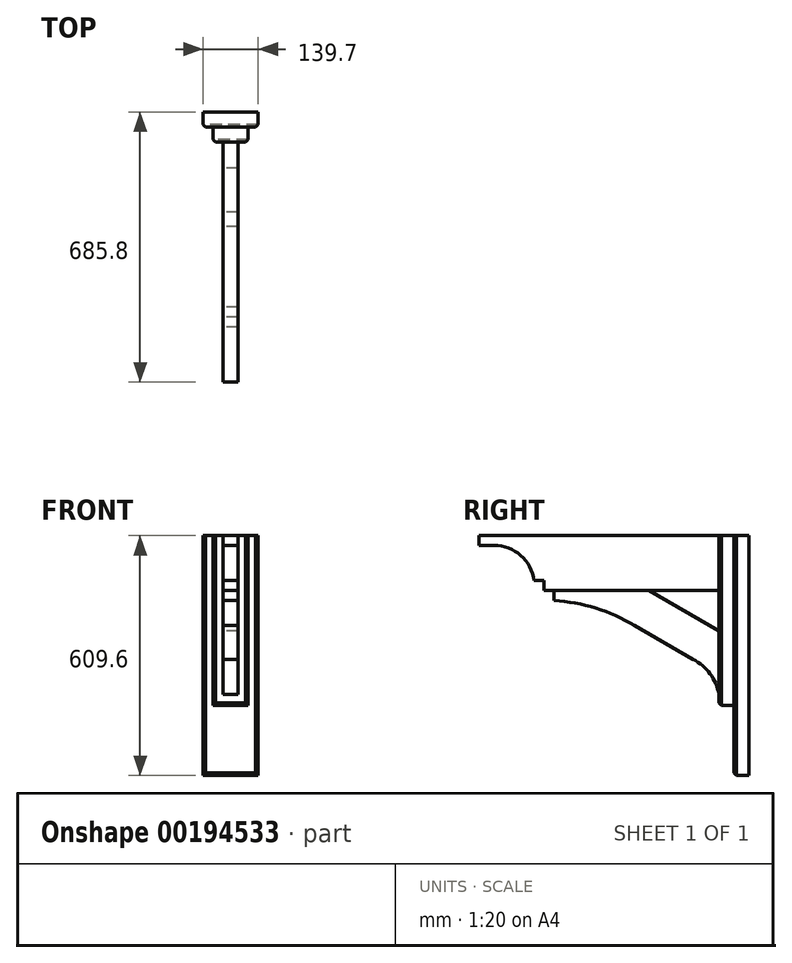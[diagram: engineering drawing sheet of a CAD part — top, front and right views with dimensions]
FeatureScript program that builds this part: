
annotation { "Feature Type Name" : "Feature", "Feature Type Description" : "" }
export const myFeature = defineFeature(function(context is Context, id is Id, definition is map)
    precondition{}
    {
        {
            var Q0;
            Q0=qCreatedBy(makeId("Front.planeOp"),FACE);
            var sketch = newSketch(context, id + "F0", { "sketchPlane" : qUnion([Q0])});
            skLineSegment(sketch, "E0.bottom", {"start": v(19.05, -69.85) * mm, "end": v(-19.05, -69.85) * mm});
            skLineSegment(sketch, "E0.top", {"start": v(19.05, 69.85) * mm, "end": v(-19.05, 69.85) * mm});
            skLineSegment(sketch, "E0.left", {"start": v(19.05, -69.85) * mm, "end": v(19.05, 69.85) * mm});
            skLineSegment(sketch, "E0.right", {"start": v(-19.05, -69.85) * mm, "end": v(-19.05, 69.85) * mm});
            skPoint(sketch, "E0.middle", {"position": v(0, 0) * mm});
            skSolve(sketch);
        }
        {
            var Q0;
            Q0=makeQuery(id+"F0.imprint","IMPRINT",FACE,{"disambiguationData":[TD([[makeQuery(id+"F0.imprint","IMPRINT",EDGE,{"derivedFrom":sQuery(id+"F0.wireOp",EDGE,"E0.bottom")}),-1.0]])]});
            extrude(context, id + "F1", {"entities" : qUnion([Q0]), "depth" : 609.6 * mm});
        }
        {
            var Q0;
            Q0=qCreatedBy(makeId("Front.planeOp"),FACE);
            var sketch = newSketch(context, id + "F2", { "sketchPlane" : qUnion([Q0])});
            skLineSegment(sketch, "E1.bottom", {"start": v(44.45, 69.85) * mm, "end": v(-44.45, 69.85) * mm});
            skLineSegment(sketch, "E1.top", {"start": v(44.45, -361.95) * mm, "end": v(-44.45, -361.95) * mm});
            skLineSegment(sketch, "E1.left", {"start": v(44.45, 69.85) * mm, "end": v(44.45, -361.95) * mm});
            skLineSegment(sketch, "E1.right", {"start": v(-44.45, 69.85) * mm, "end": v(-44.45, -361.95) * mm});
            skPoint(sketch, "E2", {"position": v(0, 69.85) * mm});
            skSolve(sketch);
        }
        {
            var Q0;
            Q0=makeQuery(id+"F2.imprint","IMPRINT",FACE,{"disambiguationData":[TD([[makeQuery(id+"F2.imprint","IMPRINT",EDGE,{"derivedFrom":sQuery(id+"F2.wireOp",EDGE,"E1.bottom")}),1.0]])]});
            extrude(context, id + "F3", {"entities" : qUnion([Q0]), "oppositeDirection" : true, "depth" : 38.1 * mm});
        }
        {
            var Q0;
            Q0=qCreatedBy(makeId("Right.planeOp"),FACE);
            var sketch = newSketch(context, id + "F4", { "sketchPlane" : qUnion([Q0])});
            skLineSegment(sketch, "E3.bottom", {"start": v(-457.2, -69.85) * mm, "end": v(0, -333.81) * mm, "construction": true});
            skLineSegment(sketch, "E3.top", {"start": v(-387.35, 51.13) * mm, "end": v(69.85, -212.83) * mm, "construction": true});
            skLineSegment(sketch, "E3.left", {"start": v(-457.2, -69.85) * mm, "end": v(-387.35, 51.13) * mm, "construction": true});
            skLineSegment(sketch, "E3.right", {"start": v(0, -333.81) * mm, "end": v(69.85, -212.83) * mm, "construction": true});
            skLineSegment(sketch, "E4", {"start": v(34.93, -273.32) * mm, "end": v(-422.28, -9.36) * mm, "construction": true});
            skLineSegment(sketch, "E5", {"start": v(-419.1, -69.85) * mm, "end": v(-177.8, -69.85) * mm});
            skLineSegment(sketch, "E6", {"start": v(0, -333.81) * mm, "end": v(0, -172.5) * mm});
            skLineSegment(sketch, "E7", {"start": v(0, -172.5) * mm, "end": v(-177.8, -69.85) * mm});
            skArc(sketch, "E8", {"start": v(0, -333.81) * mm, "mid": v(-22.62, -281.6) * mm, "end": v(-65.76, -244.52) * mm});
            skLineSegment(sketch, "E9", {"start": v(-419.1, -69.85) * mm, "end": v(-419.1, -95.25) * mm});
            skArc(sketch, "E10", {"start": v(-215, -158.36) * mm, "mid": v(-313.31, -114.71) * mm, "end": v(-419.1, -95.25) * mm});
            skLineSegment(sketch, "E11", {"start": v(-215, -158.36) * mm, "end": v(-65.76, -244.52) * mm});
            skSolve(sketch);
        }
        {
            var Q0;
            Q0=makeQuery(id+"F4.imprint","IMPRINT",FACE,{"disambiguationData":[TD([[makeQuery(id+"F4.imprint","IMPRINT",EDGE,{"derivedFrom":sQuery(id+"F4.wireOp",EDGE,"E5")}),-1.0]])]});
            extrude(context, id + "F5", {"entities" : qUnion([Q0]), "endBound" : BoundingType.SYMMETRIC, "depth" : 38.1 * mm});
        }
        {
            var Q0;
            Q0=makeQuery(id+"F3.opExtrude","CAP_FACE",FACE,{"disambiguationData":[OSD([sQuery(id+"F2.wireOp",EDGE,"E1.bottom"),sQuery(id+"F2.wireOp",EDGE,"E1.top"),sQuery(id+"F2.wireOp",EDGE,"E1.left"),sQuery(id+"F2.wireOp",EDGE,"E1.right")])],"isStart":false});
            var sketch = newSketch(context, id + "F6", { "sketchPlane" : qUnion([Q0])});
            skLineSegment(sketch, "E12.bottom", {"start": v(-69.85, 69.85) * mm, "end": v(69.85, 69.85) * mm});
            skLineSegment(sketch, "E12.top", {"start": v(-69.85, -539.75) * mm, "end": v(69.85, -539.75) * mm});
            skLineSegment(sketch, "E12.left", {"start": v(-69.85, 69.85) * mm, "end": v(-69.85, -539.75) * mm});
            skLineSegment(sketch, "E12.right", {"start": v(69.85, 69.85) * mm, "end": v(69.85, -539.75) * mm});
            skPoint(sketch, "E13", {"position": v(0, 69.85) * mm});
            skSolve(sketch);
        }
        {
            var Q0;
            Q0=makeQuery(id+"F6.imprint","IMPRINT",FACE,{"disambiguationData":[TD([[makeQuery(id+"F6.imprint","IMPRINT",EDGE,{"derivedFrom":sQuery(id+"F6.wireOp",EDGE,"E12.top")}),1.0]])]});
            var Q1;
            Q1=makeQuery(id+"F6.imprint","IMPRINT",FACE,{"disambiguationData":[TD([[makeQuery(id+"F6.imprint","IMPRINT",EDGE,{"derivedFrom":makeQuery(id+"F3.opExtrude","CAP_EDGE",EDGE,{"disambiguationData":[OSD([sQuery(id+"F2.wireOp",EDGE,"E1.top")])],"isStart":false})}),1.0]])]});
            extrude(context, id + "F7", {"entities" : qUnion([Q0, Q1]), "depth" : 38.1 * mm});
        }
        {
            var Q0;
            Q0=makeQuery(id+"F1.opExtrude","SWEPT_FACE",FACE,{"disambiguationData":[OSD([sQuery(id+"F0.wireOp",EDGE,"E0.right")])]});
            var sketch = newSketch(context, id + "F8", { "sketchPlane" : qUnion([Q0])});
            skLineSegment(sketch, "E14", {"start": v(609.6, 69.85) * mm, "end": v(609.6, 44.45) * mm});
            skArc(sketch, "E15", {"start": v(571.5, 44.45) * mm, "mid": v(503.8, 19.31) * mm, "end": v(469.9, -44.45) * mm});
            skLineSegment(sketch, "E16", {"start": v(444.5, -44.45) * mm, "end": v(444.5, -69.85) * mm});
            skLineSegment(sketch, "E17", {"start": v(444.5, -44.45) * mm, "end": v(469.9, -44.45) * mm});
            skLineSegment(sketch, "E18", {"start": v(609.6, 44.45) * mm, "end": v(571.5, 44.45) * mm});
            skSolve(sketch);
        }
        {
            var Q0;
            {var subQ0=sQuery(id+"F8.wireOp",EDGE,"E15");Q0=makeQuery(id+"F8.imprint","IMPRINT",FACE,{"disambiguationData":[TD([[makeQuery(id+"F8.imprint","IMPRINT",EDGE,{"derivedFrom":subQ0}),1.0]])]});}
            extrude(context, id + "F9", {"entities" : qUnion([Q0]), "operationType" : NewBodyOperationType.REMOVE, "endBound" : BoundingType.UP_TO_NEXT, "oppositeDirection" : true, "depth" : 25.4 * mm});
        }
        {
            var Q0;
            Q0=makeQuery(id+"F3.opExtrude","CAP_EDGE",EDGE,{"disambiguationData":[OSD([sQuery(id+"F2.wireOp",EDGE,"E1.left")])],"isStart":true});
            var Q1;
            Q1=makeQuery(id+"F3.opExtrude","CAP_EDGE",EDGE,{"disambiguationData":[OSD([sQuery(id+"F2.wireOp",EDGE,"E1.right")])],"isStart":true});
            var Q2;
            Q2=makeQuery(id+"F3.opExtrude","CAP_EDGE",EDGE,{"disambiguationData":[OSD([sQuery(id+"F2.wireOp",EDGE,"E1.top")])],"isStart":true});
            var Q3;
            Q3=makeQuery(id+"F7.opExtrude","CAP_EDGE",EDGE,{"disambiguationData":[OSD([sQuery(id+"F6.wireOp",EDGE,"E12.left")])],"isStart":true});
            var Q4;
            Q4=makeQuery(id+"F7.opExtrude","CAP_EDGE",EDGE,{"disambiguationData":[OSD([sQuery(id+"F6.wireOp",EDGE,"E12.top")])],"isStart":true});
            var Q5;
            Q5=makeQuery(id+"F7.opExtrude","CAP_EDGE",EDGE,{"disambiguationData":[OSD([sQuery(id+"F6.wireOp",EDGE,"E12.right")])],"isStart":true});
            chamfer(context, id + "F10", {"entities" : qUnion([Q0, Q1, Q2, Q3, Q4, Q5]), "width" : 6.35 * mm, "tangentPropagation" : true});
        }
    });
